# Revit family: Furniture-Mirror_Cabinet-KOHLER-K-56551_1
name_source: partatom
category: Casework
units: mm (PartAtom-declared; Revit-internal decimal feet)

## family parameters
Cut with Voids When Loaded = No
Host = Face
OmniClass Number = 23.21.19.00
OmniClass Title = Casework
Room Calculation Point = No
Shared = No

## types (1)
- NA-Not Applicable
    ADA Compliant = No
    Assembly Code = E2010.30
    Date Modified = 06/28/2023
    Default Elevation = 60"
    Depth = 4 15/16"
    Description = CL REFRESH 20 INCH X 36 INCH DUAL MOUNT GOOD
    Finish = Kohler-Metal-V-Matte_Silver
    Hardware Included = No
    Height = 36"
    Manufacturer = Kohler Co.
    Master Format 2014 = 12 35 30.23
    Master Format 2014 Name = Bathroom Casework
    Material = Aluminium
    Model = K-56551-NA
    Product Documentation Link = https://www.us.kohler.com
    Product Finish = Kohler-Metal-V-Matte_Silver
    Product Page URL = http://www.us.kohler.com
    Type = 1
    URL = https://www.us.kohler.com
    WaterSense Certified = No
    Width = 20"

## geometry (parser evidence)
native form markers: Sweep x5
no freeform markers — native parametric forms only
